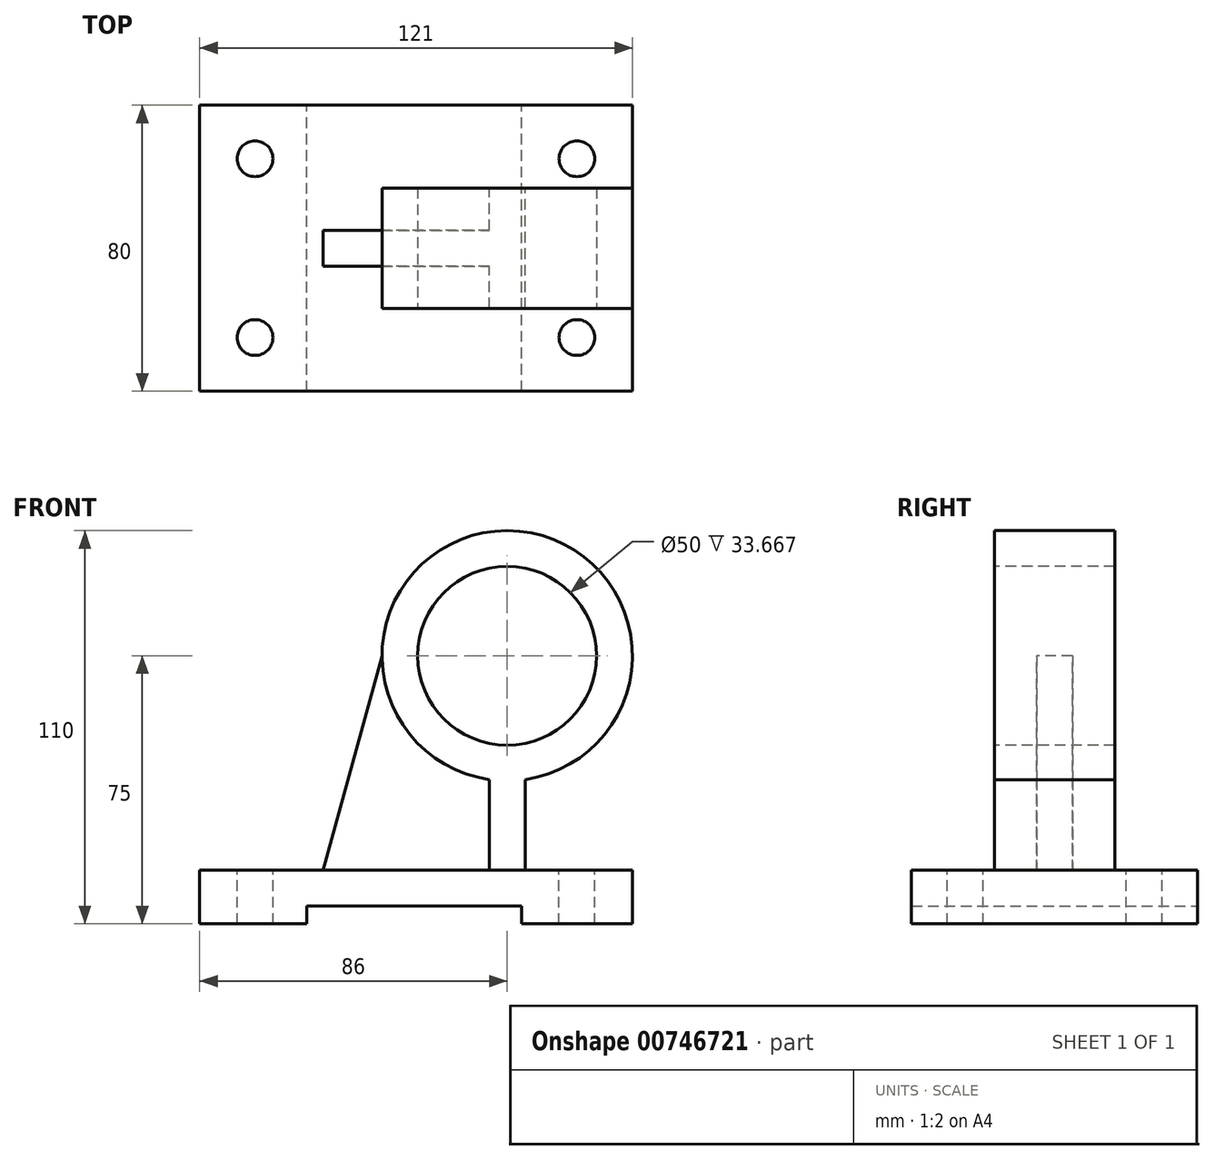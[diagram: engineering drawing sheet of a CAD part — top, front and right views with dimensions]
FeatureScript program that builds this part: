
annotation { "Feature Type Name" : "Feature", "Feature Type Description" : "" }
export const myFeature = defineFeature(function(context is Context, id is Id, definition is map)
    precondition{}
    {
        {
            var Q0;
            Q0=qCreatedBy(makeId("Front.planeOp"),FACE);
            var sketch = newSketch(context, id + "F0", { "sketchPlane" : qUnion([Q0])});
            skLineSegment(sketch, "E0", {"start": v(0, 0) * mm, "end": v(121, 0) * mm});
            skLineSegment(sketch, "E1", {"start": v(121, 0) * mm, "end": v(121, -15) * mm});
            skLineSegment(sketch, "E2", {"start": v(121, -15) * mm, "end": v(90, -15) * mm});
            skLineSegment(sketch, "E3", {"start": v(30, -10) * mm, "end": v(30, -15) * mm});
            skLineSegment(sketch, "E4", {"start": v(30, -15) * mm, "end": v(0, -15) * mm});
            skLineSegment(sketch, "E5", {"start": v(0, -15) * mm, "end": v(0, 0) * mm});
            skLineSegment(sketch, "E6", {"start": v(90, -15) * mm, "end": v(90, -10) * mm});
            skLineSegment(sketch, "E7", {"start": v(30, -10) * mm, "end": v(90, -10) * mm});
            skSolve(sketch);
        }
        {
            var Q0;
            Q0=qSketchRegion(id+"F0",true);
            extrude(context, id + "F1", {"entities" : qUnion([Q0]), "depth" : 80 * mm, "offsetDistance" : 25 * mm});
        }
        {
            var Q0;
            Q0=makeQuery(id+"F1.opExtrude","SWEPT_FACE",FACE,{"disambiguationData":[OSD([sQuery(id+"F0.wireOp",EDGE,"E0")])]});
            var sketch = newSketch(context, id + "F2", { "sketchPlane" : qUnion([Q0])});
            skCircle(sketch, "E8", {"center": v(15.5, -15) * mm, "radius": 5 * mm});
            skCircle(sketch, "E9", {"center": v(15.5, -65) * mm, "radius": 5 * mm});
            skCircle(sketch, "E10", {"center": v(105.5, -65) * mm, "radius": 5 * mm});
            skCircle(sketch, "E11", {"center": v(105.5, -15) * mm, "radius": 5 * mm});
            skPoint(sketch, "E12", {"position": v(60.5, -40) * mm});
            skPoint(sketch, "E12.positionSnap0", {"position": v(0, -40) * mm});
            skPoint(sketch, "E12.positionSnap1", {"position": v(60.5, 0) * mm});
            skLineSegment(sketch, "E13", {"start": v(0, -40) * mm, "end": v(121, -40) * mm});
            skLineSegment(sketch, "E14", {"start": v(60.5, 0) * mm, "end": v(60.5, -80) * mm});
            skSolve(sketch);
        }
        {
            var Q0;
            Q0=qSketchRegion(id+"F2",true);
            extrude(context, id + "F3", {"entities" : qUnion([Q0]), "operationType" : NewBodyOperationType.REMOVE, "oppositeDirection" : true, "depth" : 25 * mm, "offsetDistance" : 25 * mm});
        }
        {
            var Q0;
            Q0=makeQuery(id+"F1.opExtrude","SWEPT_FACE",FACE,{"disambiguationData":[OSD([sQuery(id+"F0.wireOp",EDGE,"E0")])]});
            var sketch = newSketch(context, id + "F4", { "sketchPlane" : qUnion([Q0])});
            skLineSegment(sketch, "E15", {"start": v(0, -40) * mm, "end": v(62.75, -40) * mm, "construction": true});
            skLineSegment(sketch, "E16.bottom", {"start": v(81, -45) * mm, "end": v(34.5, -45) * mm});
            skLineSegment(sketch, "E16.top", {"start": v(81, -35) * mm, "end": v(34.5, -35) * mm});
            skLineSegment(sketch, "E16.left", {"start": v(91, -45) * mm, "end": v(91, -35) * mm});
            skLineSegment(sketch, "E16.right", {"start": v(34.5, -45) * mm, "end": v(34.5, -35) * mm});
            skPoint(sketch, "E16.middle", {"position": v(62.75, -40) * mm});
            skLineSegment(sketch, "E17.bottom", {"start": v(91, -56.83) * mm, "end": v(81, -56.83) * mm});
            skLineSegment(sketch, "E17.top", {"start": v(91, -23.17) * mm, "end": v(81, -23.17) * mm});
            skLineSegment(sketch, "E17.left", {"start": v(91, -56.83) * mm, "end": v(91, -23.17) * mm});
            skLineSegment(sketch, "E17.right", {"start": v(81, -56.83) * mm, "end": v(81, -45) * mm});
            skPoint(sketch, "E17.middle", {"position": v(86, -40) * mm});
            skPoint(sketch, "E17.cornerSnap0", {"position": v(91, -40) * mm});
            skLineSegment(sketch, "E18.trimOffspring", {"start": v(81, -35) * mm, "end": v(81, -23.17) * mm});
            skLineSegment(sketch, "E19.trimOffspring", {"start": v(86, -40) * mm, "end": v(121, -40) * mm, "construction": true});
            skSolve(sketch);
        }
        {
            var Q0;
            Q0=makeQuery(id+"F4.imprint","IMPRINT",FACE,{"disambiguationData":[TD([[makeQuery(id+"F4.imprint","IMPRINT",EDGE,{"derivedFrom":sQuery(id+"F4.wireOp",EDGE,"E16.bottom")}),-1.0]])]});
            extrude(context, id + "F5", {"entities" : qUnion([Q0]), "operationType" : NewBodyOperationType.ADD, "depth" : 60 * mm, "offsetDistance" : 25 * mm});
        }
        {
            var Q0;
            Q0=makeQuery(id+"F5.opExtrude","SWEPT_FACE",FACE,{"disambiguationData":[OSD([sQuery(id+"F4.wireOp",EDGE,"E17.bottom")])]});
            var sketch = newSketch(context, id + "F6", { "sketchPlane" : qUnion([Q0])});
            skCircle(sketch, "E20", {"center": v(86, 60) * mm, "radius": 35 * mm});
            skSolve(sketch);
        }
        {
            var Q0;
            Q0=qSketchRegion(id+"F6",true);
            var Q1;
            Q1=makeQuery(id+"F5.opExtrude","SWEPT_FACE",FACE,{"disambiguationData":[OSD([sQuery(id+"F4.wireOp",EDGE,"E17.top")])]});
            extrude(context, id + "F7", {"entities" : qUnion([Q0]), "operationType" : NewBodyOperationType.ADD, "endBound" : BoundingType.UP_TO_SURFACE, "oppositeDirection" : true, "depth" : 25 * mm, "endBoundEntityFace" : qUnion([Q1]), "offsetDistance" : 25 * mm});
        }
        {
            var Q0;
            Q0=makeQuery(id+"F7.boolean.opBoolean","MERGE",FACE,{"derivedFrom":[makeQuery(id+"F5.opExtrude","SWEPT_FACE",FACE,{"disambiguationData":[OSD([sQuery(id+"F4.wireOp",EDGE,"E17.bottom")])]}),makeQuery(id+"F7.opExtrude","CAP_FACE",FACE,{"disambiguationData":[OSD([sQuery(id+"F6.wireOp",EDGE,"E20")])],"isStart":true})]});
            var sketch = newSketch(context, id + "F8", { "sketchPlane" : qUnion([Q0])});
            skCircle(sketch, "E21", {"center": v(86, 60) * mm, "radius": 25 * mm});
            skSolve(sketch);
        }
        {
            var Q0;
            Q0=makeQuery(id+"F8.imprint","IMPRINT",FACE,{"disambiguationData":[TD([[makeQuery(id+"F8.imprint","IMPRINT",EDGE,{"derivedFrom":sQuery(id+"F8.wireOp",EDGE,"E21")}),1.0]])]});
            extrude(context, id + "F9", {"entities" : qUnion([Q0]), "operationType" : NewBodyOperationType.REMOVE, "oppositeDirection" : true, "depth" : 52.6 * mm, "offsetDistance" : 25 * mm});
        }
        {
            var Q0;
            Q0=makeQuery(id+"F5.opExtrude","SWEPT_FACE",FACE,{"disambiguationData":[OSD([sQuery(id+"F4.wireOp",EDGE,"E16.bottom")])]});
            var sketch = newSketch(context, id + "F10", { "sketchPlane" : qUnion([Q0])});
            skLineSegment(sketch, "E22", {"start": v(34.5, 0) * mm, "end": v(51, 60) * mm});
            skLineSegment(sketch, "E23", {"start": v(51, 60) * mm, "end": v(34.5, 60) * mm});
            skLineSegment(sketch, "E24", {"start": v(34.5, 60) * mm, "end": v(34.5, 0) * mm});
            skSolve(sketch);
        }
        {
            var Q0;
            Q0=makeQuery(id+"F10.imprint","IMPRINT",FACE,{"disambiguationData":[TD([[makeQuery(id+"F10.imprint","IMPRINT",EDGE,{"derivedFrom":sQuery(id+"F10.wireOp",EDGE,"E22")}),1.0]])]});
            extrude(context, id + "F11", {"entities" : qUnion([Q0]), "operationType" : NewBodyOperationType.REMOVE, "oppositeDirection" : true, "depth" : 25 * mm, "offsetDistance" : 25 * mm});
        }
    });
